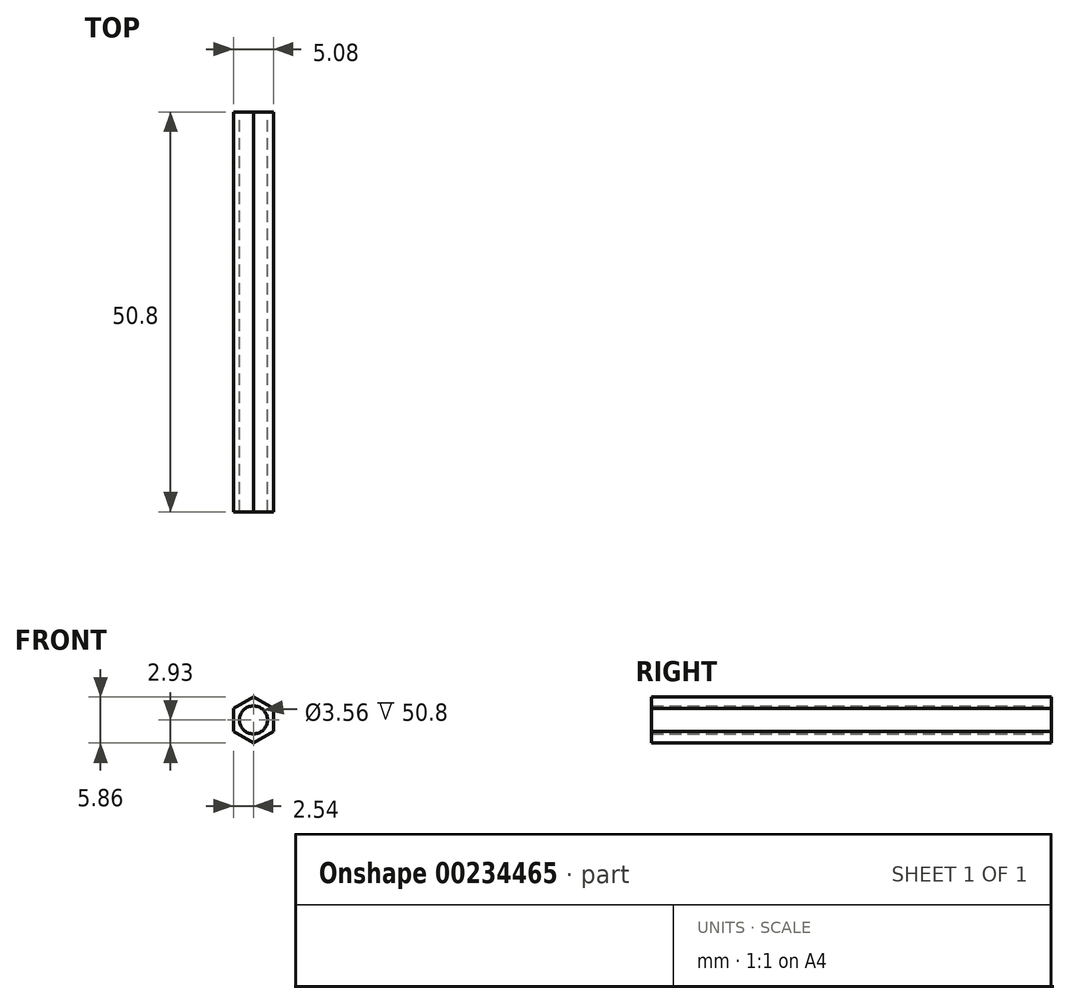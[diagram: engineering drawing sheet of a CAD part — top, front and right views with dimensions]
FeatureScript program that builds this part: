
annotation { "Feature Type Name" : "Feature", "Feature Type Description" : "" }
export const myFeature = defineFeature(function(context is Context, id is Id, definition is map)
    precondition{}
    {
        {
            var Q0;
            Q0=qCreatedBy(makeId("Front.planeOp"),FACE);
            var sketch = newSketch(context, id + "F0", { "sketchPlane" : qUnion([Q0])});
            skCircle(sketch, "E0", {"center": v(0, 0) * mm, "radius": 1.78 * mm});
            skCircle(sketch, "E1.cCircle", {"center": v(0, 0) * mm, "radius": 2.54 * mm, "construction": true});
            skLineSegment(sketch, "E1.0", {"start": v(2.54, 1.47) * mm, "end": v(2.54, -1.47) * mm});
            skLineSegment(sketch, "E1.1", {"start": v(2.54, -1.47) * mm, "end": v(0, -2.93) * mm});
            skLineSegment(sketch, "E1.2", {"start": v(0, -2.93) * mm, "end": v(-2.54, -1.47) * mm});
            skLineSegment(sketch, "E1.3", {"start": v(-2.54, -1.47) * mm, "end": v(-2.54, 1.47) * mm});
            skLineSegment(sketch, "E1.4", {"start": v(-2.54, 1.47) * mm, "end": v(0, 2.93) * mm});
            skLineSegment(sketch, "E1.5", {"start": v(0, 2.93) * mm, "end": v(2.54, 1.47) * mm});
            skPoint(sketch, "E1.0.midPoint", {"position": v(2.54, 0) * mm});
            skSolve(sketch);
        }
        {
            var Q0;
            Q0=makeQuery(id+"F0.imprint","IMPRINT",FACE,{"disambiguationData":[TD([[makeQuery(id+"F0.imprint","IMPRINT",EDGE,{"derivedFrom":sQuery(id+"F0.wireOp",EDGE,"E0")}),-1.0]])]});
            extrude(context, id + "F1", {"entities" : qUnion([Q0]), "depth" : 50.8 * mm});
        }
    });
